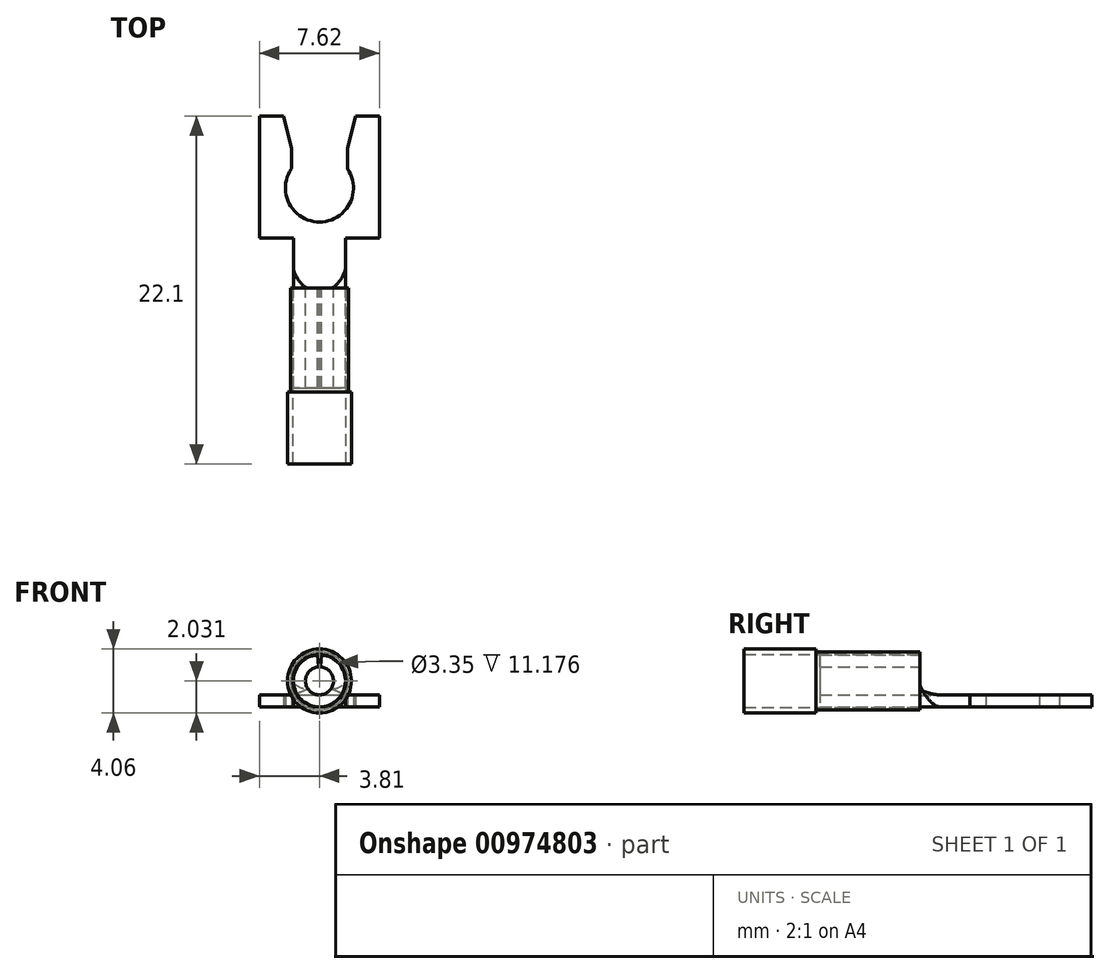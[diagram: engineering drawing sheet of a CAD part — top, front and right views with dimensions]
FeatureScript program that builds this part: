
annotation { "Feature Type Name" : "Feature", "Feature Type Description" : "" }
export const myFeature = defineFeature(function(context is Context, id is Id, definition is map)
    precondition{}
    {
        {
            var Q0;
            Q0=qCreatedBy(makeId("Top.planeOp"),FACE);
            var sketch = newSketch(context, id + "F0", { "sketchPlane" : qUnion([Q0])});
            skLineSegment(sketch, "E0.bottom", {"start": v(-3.81, 4.57) * mm, "end": v(-2.29, 4.57) * mm});
            skLineSegment(sketch, "E0.top", {"start": v(-3.8, -3.18) * mm, "end": v(3.81, -3.18) * mm});
            skLineSegment(sketch, "E0.left", {"start": v(-3.81, 4.57) * mm, "end": v(-3.81, -3.18) * mm});
            skLineSegment(sketch, "E0.right", {"start": v(3.8, 4.57) * mm, "end": v(3.81, -3.17) * mm});
            skArc(sketch, "E1", {"start": v(-1.78, 1.22) * mm, "mid": v(0, -2.16) * mm, "end": v(1.78, 1.22) * mm});
            skLineSegment(sketch, "E2.bottom", {"start": v(-1.65, -3.18) * mm, "end": v(1.65, -3.17) * mm});
            skLineSegment(sketch, "E2.top", {"start": v(-1.65, -5.08) * mm, "end": v(1.65, -5.08) * mm});
            skLineSegment(sketch, "E2.left", {"start": v(-1.65, -3.18) * mm, "end": v(-1.65, -5.08) * mm});
            skLineSegment(sketch, "E2.right", {"start": v(1.65, -3.18) * mm, "end": v(1.65, -5.08) * mm});
            skPoint(sketch, "E3", {"position": v(0, -3.18) * mm});
            skLineSegment(sketch, "E4.trimOffspring", {"start": v(2.29, 4.57) * mm, "end": v(3.81, 4.57) * mm});
            skLineSegment(sketch, "E5", {"start": v(-2.29, 4.57) * mm, "end": v(-1.78, 2.5) * mm});
            skLineSegment(sketch, "E6", {"start": v(-1.78, 2.5) * mm, "end": v(-1.78, 1.22) * mm});
            skLineSegment(sketch, "E7", {"start": v(2.29, 4.57) * mm, "end": v(1.78, 2.5) * mm});
            skLineSegment(sketch, "E8", {"start": v(1.78, 2.5) * mm, "end": v(1.78, 1.22) * mm});
            skLineSegment(sketch, "E9", {"start": v(-1.78, 1.22) * mm, "end": v(1.78, 1.22) * mm, "construction": true});
            skSolve(sketch);
        }
        {
            var Q0;
            Q0=qSketchRegion(id+"F0",true);
            extrude(context, id + "F1", {"entities" : qUnion([Q0]), "depth" : 0.76 * mm, "offsetDistance" : 25.4 * mm});
        }
        {
            var Q0;
            {var subQ0=sQuery(id+"F0.wireOp",EDGE,"E2.left");var subQ1=sQuery(id+"F0.wireOp",EDGE,"E2.top");var subQ2=makeQuery(id+"F1.opExtrude","SWEPT_FACE",FACE,{"disambiguationData":[OSD([subQ1])]});Q0=makeQuery(id+"F4.boolean.opBoolean","SPLIT",FACE,{"disambiguationData":[TD([makeQuery(id+"F1.opExtrude","SWEPT_FACE",FACE,{"disambiguationData":[OSD([subQ0])]})])],"derivedFrom":subQ2});}
            cPlane(context, id + "F2", {"entities" : qUnion([Q0]), "cplaneType" : CPlaneType.OFFSET, "offset" : 1.27 * mm, "width" : 152.4 * mm, "height" : 152.4 * mm});
        }
        {
            var Q0;
            Q0=qCreatedBy(id+"F2.planeOp",FACE);
            var sketch = newSketch(context, id + "F3", { "sketchPlane" : qUnion([Q0])});
            skArc(sketch, "E10", {"start": v(-0.13, 3.3) * mm, "mid": v(0, 0) * mm, "end": v(0.13, 3.3) * mm});
            skArc(sketch, "E11", {"start": v(-0.07, 2.54) * mm, "mid": v(0, 0.76) * mm, "end": v(0.07, 2.54) * mm});
            skLineSegment(sketch, "E12", {"start": v(0, 1.65) * mm, "end": v(0, 0) * mm, "construction": true});
            skLineSegment(sketch, "E13", {"start": v(0.07, 2.54) * mm, "end": v(0.13, 3.3) * mm});
            skLineSegment(sketch, "E14", {"start": v(-0.07, 2.54) * mm, "end": v(-0.13, 3.3) * mm});
            skLineSegment(sketch, "E15", {"start": v(-0.07, 2.54) * mm, "end": v(0.07, 2.54) * mm, "construction": true});
            skLineSegment(sketch, "E16", {"start": v(-0.13, 3.3) * mm, "end": v(0.13, 3.3) * mm, "construction": true});
            skLineSegment(sketch, "E17", {"start": v(0, 1.65) * mm, "end": v(-0.07, 2.54) * mm, "construction": true});
            skSolve(sketch);
        }
        {
            var Q0;
            Q0=qSketchRegion(id+"F3",true);
            extrude(context, id + "F4", {"entities" : qUnion([Q0]), "operationType" : NewBodyOperationType.ADD, "depth" : 6.35 * mm, "offsetDistance" : 25.4 * mm});
        }
        {
            var Q0;
            Q0=makeQuery(id+"F4.opExtrude","CAP_FACE",FACE,{"disambiguationData":[OSD([sQuery(id+"F3.wireOp",EDGE,"E10"),sQuery(id+"F3.wireOp",EDGE,"E11"),sQuery(id+"F3.wireOp",EDGE,"E13"),sQuery(id+"F3.wireOp",EDGE,"E14")])],"isStart":true});
            var sketch = newSketch(context, id + "F5", { "sketchPlane" : qUnion([Q0])});
            skPoint(sketch, "E18.orphan", {"position": v(2.16, 0.76) * mm});
            skPoint(sketch, "E19.orphan", {"position": v(-2.16, 0.76) * mm});
            skPoint(sketch, "E20.orphan", {"position": v(0.13, 3.3) * mm});
            skPoint(sketch, "E21.orphan", {"position": v(0.07, 2.54) * mm});
            skPoint(sketch, "E22.orphan", {"position": v(-0.07, 2.54) * mm});
            skPoint(sketch, "E23.orphan", {"position": v(-0.13, 3.3) * mm});
            skLineSegment(sketch, "E24", {"start": v(0.73, 1.14) * mm, "end": v(-0.73, 1.14) * mm, "construction": true});
            skLineSegment(sketch, "E25", {"start": v(1.65, 1.52) * mm, "end": v(-1.65, 1.52) * mm, "construction": true});
            skLineSegment(sketch, "E26", {"start": v(0, 1.65) * mm, "end": v(0, 1.52) * mm, "construction": true});
            skArc(sketch, "E27", {"start": v(0.73, 1.14) * mm, "mid": v(1.23, 1.24) * mm, "end": v(1.65, 1.52) * mm});
            skArc(sketch, "E28", {"start": v(-1.65, 1.52) * mm, "mid": v(-1.23, 1.24) * mm, "end": v(-0.73, 1.14) * mm});
            skArc(sketch, "E29.0", {"start": v(0.13, 3.3) * mm, "mid": v(0, 0) * mm, "end": v(-0.13, 3.3) * mm, "construction": true});
            skSolve(sketch);
        }
        {
            var Q0;
            Q0=makeQuery(id+"F1.opExtrude","SWEPT_FACE",FACE,{"disambiguationData":[OSD([sQuery(id+"F0.wireOp",EDGE,"E2.top")])]});
            var Q1;
            {var subQ0=sQuery(id+"F5.wireOp",EDGE,"E27");Q1=makeQuery(id+"F5.imprint","IMPRINT",FACE,{"disambiguationData":[TD([[makeQuery(id+"F5.imprint","IMPRINT",EDGE,{"derivedFrom":subQ0}),-1.0]])]});}
            loft(context, id + "F6", {"operationType" : NewBodyOperationType.ADD, "startCondition" : LoftEndDerivativeType.NORMAL_TO_PROFILE, "startMagnitude" : 1, "endCondition" : LoftEndDerivativeType.TANGENT_TO_PROFILE, "endMagnitude" : 1, "sheetProfilesArray" : [{ "sheetProfileEntities" : qUnion([Q0]) }, { "sheetProfileEntities" : qUnion([Q1]) }]});
        }
        {
            var Q0;
            {var subQ0=sQuery(id+"F3.wireOp",EDGE,"E11");var subQ2=sQuery(id+"F3.wireOp",EDGE,"E10");var subQ5=sQuery(id+"F3.wireOp",EDGE,"E14");Q0=makeQuery(id+"F6.boolean.opBoolean","SPLIT",FACE,{"disambiguationData":[TD([makeQuery(id+"F4.opExtrude","SWEPT_FACE",FACE,{"disambiguationData":[OSD([subQ5])]})])],"derivedFrom":makeQuery(id+"F4.opExtrude","CAP_FACE",FACE,{"disambiguationData":[OSD([subQ2,subQ0,sQuery(id+"F3.wireOp",EDGE,"E13"),subQ5])],"isStart":true})});}
            var sketch = newSketch(context, id + "F7", { "sketchPlane" : qUnion([Q0])});
            skArc(sketch, "E30.0", {"start": v(1.65, 1.52) * mm, "mid": v(1.25, 2.73) * mm, "end": v(0.13, 3.3) * mm, "construction": true});
            skCircle(sketch, "E31", {"center": v(0, 1.65) * mm, "radius": 1.68 * mm});
            skCircle(sketch, "E32", {"center": v(0, 1.65) * mm, "radius": 1.84 * mm});
            skSolve(sketch);
        }
        {
            var Q0;
            Q0=qSketchRegion(id+"F7",true);
            extrude(context, id + "F8", {"entities" : qUnion([Q0]), "oppositeDirection" : true, "depth" : 11.18 * mm, "offsetDistance" : 25.4 * mm});
        }
        {
            var Q0;
            Q0=makeQuery(id+"F8.opExtrude","CAP_FACE",FACE,{"disambiguationData":[OSD([sQuery(id+"F7.wireOp",EDGE,"E31"),sQuery(id+"F7.wireOp",EDGE,"E32")])],"isStart":false});
            var sketch = newSketch(context, id + "F9", { "sketchPlane" : qUnion([Q0])});
            skCircle(sketch, "E33.0", {"center": v(0, 1.65) * mm, "radius": 1.68 * mm});
            skCircle(sketch, "E34", {"center": v(0, 1.65) * mm, "radius": 2.03 * mm});
            skSolve(sketch);
        }
        {
            var Q0;
            Q0=qSketchRegion(id+"F9",true);
            extrude(context, id + "F10", {"entities" : qUnion([Q0]), "operationType" : NewBodyOperationType.ADD, "oppositeDirection" : true, "depth" : 4.57 * mm, "offsetDistance" : 25.4 * mm});
        }
    });
